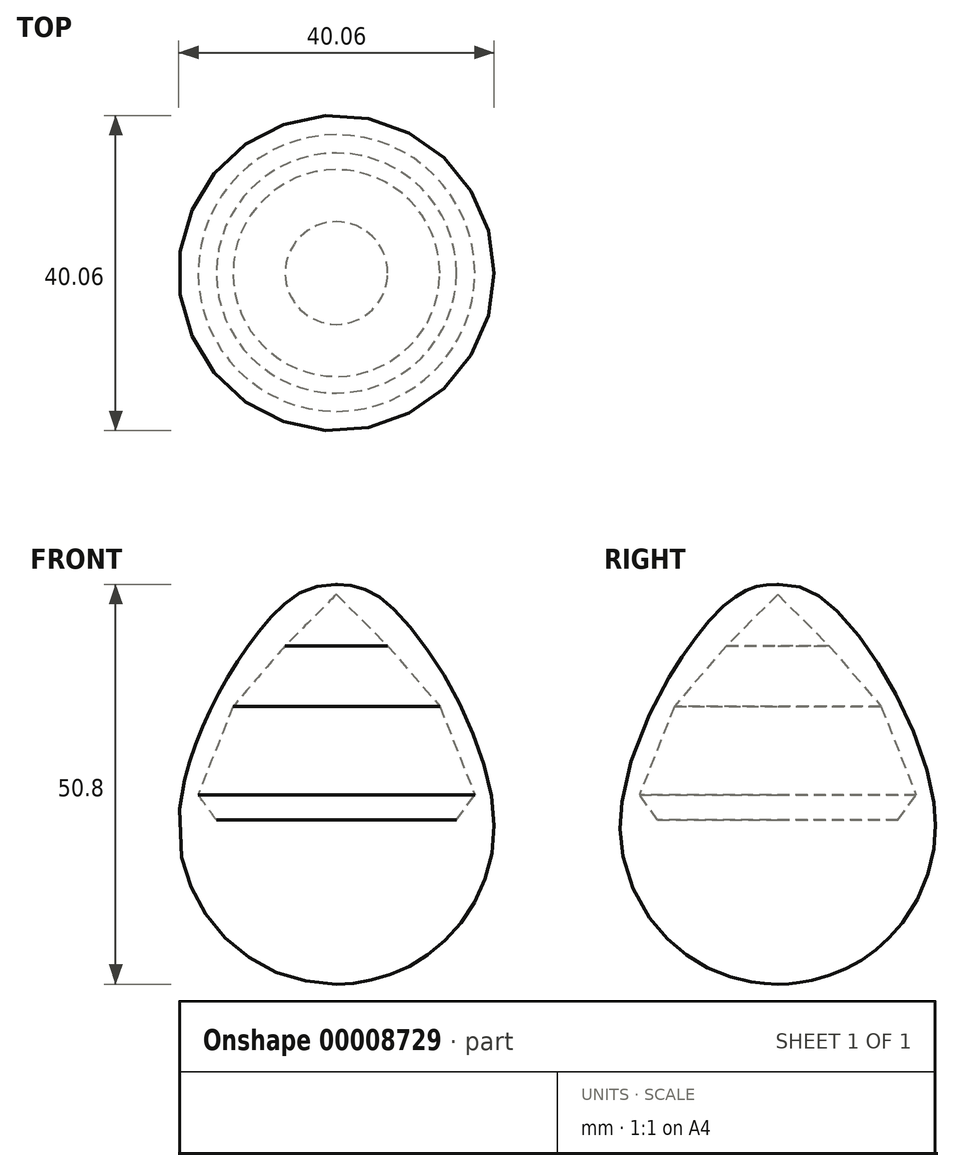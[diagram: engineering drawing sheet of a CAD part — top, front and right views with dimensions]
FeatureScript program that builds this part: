
annotation { "Feature Type Name" : "Feature", "Feature Type Description" : "" }
export const myFeature = defineFeature(function(context is Context, id is Id, definition is map)
    precondition{}
    {
        {
            var Q0;
            Q0=qCreatedBy(makeId("Front.planeOp"),FACE);
            var sketch = newSketch(context, id + "F0", { "sketchPlane" : qUnion([Q0])});
            skLineSegment(sketch, "E0", {"start": v(0, 0) * mm, "end": v(0, 69.22) * mm, "construction": true});
            skFitSpline(sketch, "E1", {"points": [v(0, 0) * mm, v(11.45, 3.6) * mm, v(20.02, 20.84) * mm, v(7.5, 47.43) * mm, v(0, 50.8) * mm], "startDerivative": vector(47.95, 0) * mm, "endDerivative": vector(-44.76, -0.47) * mm});
            skLineSegment(sketch, "E2", {"start": v(0, 0) * mm, "end": v(0, 20.84) * mm});
            skLineSegment(sketch, "E3", {"start": v(0, 20.84) * mm, "end": v(15.25, 20.84) * mm});
            skLineSegment(sketch, "E4", {"start": v(6.51, 42.98) * mm, "end": v(0, 49.5) * mm});
            skLineSegment(sketch, "E5", {"start": v(0, 49.5) * mm, "end": v(0, 50.8) * mm});
            skLineSegment(sketch, "E6", {"start": v(6.51, 42.98) * mm, "end": v(13.13, 35.29) * mm});
            skLineSegment(sketch, "E7", {"start": v(13.13, 35.29) * mm, "end": v(17.57, 24.06) * mm});
            skLineSegment(sketch, "E8", {"start": v(17.57, 24.06) * mm, "end": v(15.25, 20.84) * mm});
            skSolve(sketch);
        }
        {
            var Q0;
            Q0=makeQuery(id+"F0.imprint","IMPRINT",FACE,{"disambiguationData":[TD([[makeQuery(id+"F0.imprint","IMPRINT",EDGE,{"derivedFrom":sQuery(id+"F0.wireOp",EDGE,"E1")}),1.0]])]});
            var Q1;
            Q1=sQuery(id+"F0.wireOp",EDGE,"E0");
            revolve(context, id + "F1", {"entities" : qUnion([Q0]), "axis" : qUnion([Q1]), "revolveType" : RevolveType.FULL});
        }
    });
